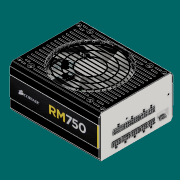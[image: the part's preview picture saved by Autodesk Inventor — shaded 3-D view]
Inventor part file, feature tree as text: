
AUTODESK INVENTOR PART (.ipt)
format: ipt  version: 2016 SP1 (Build 200210100, 210)  size: 27,194,880 bytes
history: native  units: mm
features: other x72, sketch x4
ambient origin geometry x8: Origin, YZ Plane, XZ Plane, XY Plane, X Axis, Y Axis, Z Axis, Center Point
bodies: Solid1 (feature_tree), Solid2 (feature_tree), Solid3 (feature_tree), Solid4 (feature_tree), Solid5 (feature_tree), Solid6 (feature_tree), Solid7 (feature_tree), Solid8 (feature_tree), Solid9 (feature_tree), Solid10 (feature_tree), Solid11 (feature_tree), Solid12 (feature_tree), Solid13 (feature_tree), Solid14 (feature_tree), Solid15 (feature_tree), Solid16 (feature_tree), Solid17 (feature_tree), Solid18 (feature_tree), Solid19 (feature_tree), Solid20 (feature_tree), Solid21 (feature_tree), Solid22 (feature_tree), Solid23 (feature_tree), Solid24 (feature_tree), Solid25 (feature_tree), Solid26 (feature_tree), Solid27 (feature_tree), Solid28 (feature_tree), Solid29 (feature_tree), Solid30 (feature_tree), Solid31 (feature_tree), Solid32 (feature_tree), Solid33 (feature_tree), Solid34 (feature_tree), Solid35 (feature_tree), Solid36 (feature_tree), Solid37 (feature_tree), Solid38 (feature_tree), Solid39 (feature_tree), Solid40 (feature_tree), Solid41 (feature_tree), Solid42 (feature_tree), Solid43 (feature_tree), Solid44 (feature_tree), Solid45 (feature_tree), Solid46 (feature_tree), Solid47 (feature_tree), Solid48 (feature_tree), Solid49 (feature_tree), Solid50 (feature_tree), Solid51 (feature_tree), Solid52 (feature_tree), Solid53 (feature_tree), Solid54 (feature_tree), Solid55 (feature_tree), Solid56 (feature_tree), Solid57 (feature_tree), Solid58 (feature_tree), Solid59 (feature_tree), Solid60 (feature_tree), Solid61 (feature_tree), Solid62 (feature_tree), Solid63 (feature_tree), Solid64 (feature_tree)
feature tree (76):
  other  "Decal1"
  other  "Decal2"
  other  "Decal3"
  other  "Decal4"
  sketch  "Sketch1"
  other  "Image1"
  sketch  "Sketch2"
  other  "Image2"
  sketch  "Sketch3"
  other  "Image3"
  sketch  "Sketch4"
  other  "Image4"
  other  "Lower Chassis:1"
  other  "Upper Chassis:1"
  other  "240V Kettle Plug:1"
  other  "240V Kettle Plug:2"
  other  "240V Kettle Plug:3"
  other  "240V Kettle Plug:4"
  other  "10-Pin:1"
  other  "14-Pin:1"
  other  "6-Pin:1"
  other  "6-Pin:2"
  other  "6-Pin:3"
  other  "6-Pin:4"
  other  "8-Pin:1"
  other  "8-Pin:2"
  other  "8-Pin:3"
  other  "Rocker Frame:1"
  other  "Rocker:1"
  other  "Side Sticker:1"
  other  "Side Sticker:2"
  other  "Fan Grill:1"
  other  "Fan Grill:2"
  other  "Fan Grill:3"
  other  "Fan Grill:4"
  other  "Fan Grill:5"
  other  "Fan Grill:6"
  other  "Fan Grill:7"
  other  "Fan Grill:8"
  other  "Fan Grill:9"
  other  "Fan Grill:10"
  other  "Fan Grill:11"
  other  "Fan Grill:12"
  other  "Fan Grill:13"
  other  "Fan Grill:14"
  other  "Fan Grill:15"
  other  "Fan Grill:16"
  other  "Fan Grill:17"
  other  "Fan Grill:18"
  other  "Fan Grill:19"
  other  "Fan Grill:20"
  other  "Corsair Air Series 140 Fan Frame:1"
  other  "Corsair Air Series 140 Fan Frame:2"
  other  "Corsair Air Series 140 Fan Frame:3"
  other  "Corsair Air Series 140 Fan Frame:4"
  other  "Corsair Air Series 140 Fan Frame:5"
  other  "Corsair Air Series 140 Fan Frame:6"
  other  "Corsair Air Series SP140 Fanblade:1"
  other  "Rear Sticker:1"
  other  "Copy of Internals^Corsair RM750:1"
  other  "Copy of Internals^Corsair RM750:2"
  other  "Copy of Internals^Corsair RM750:3"
  other  "Copy of Internals^Corsair RM750:4"
  other  "Copy of Internals^Corsair RM750:5"
  other  "Copy of Internals^Corsair RM750:6"
  other  "Copy of Internals^Corsair RM750:7"
  other  "Copy of Internals^Corsair RM750:8"
  other  "Copy of Internals^Corsair RM750:9"
  other  "Copy of Internals^Corsair RM750:10"
  other  "Copy of Internals^Corsair RM750:11"
  other  "Corsair Link 4-pin:1"
  other  "Corsair Link 4-pin:2"
  other  "Corsair Link 4-pin:3"
  other  "Corsair Link 4-pin:4"
  other  "Corsair Link 4-pin:5"
  other  "_N_A_:1"
